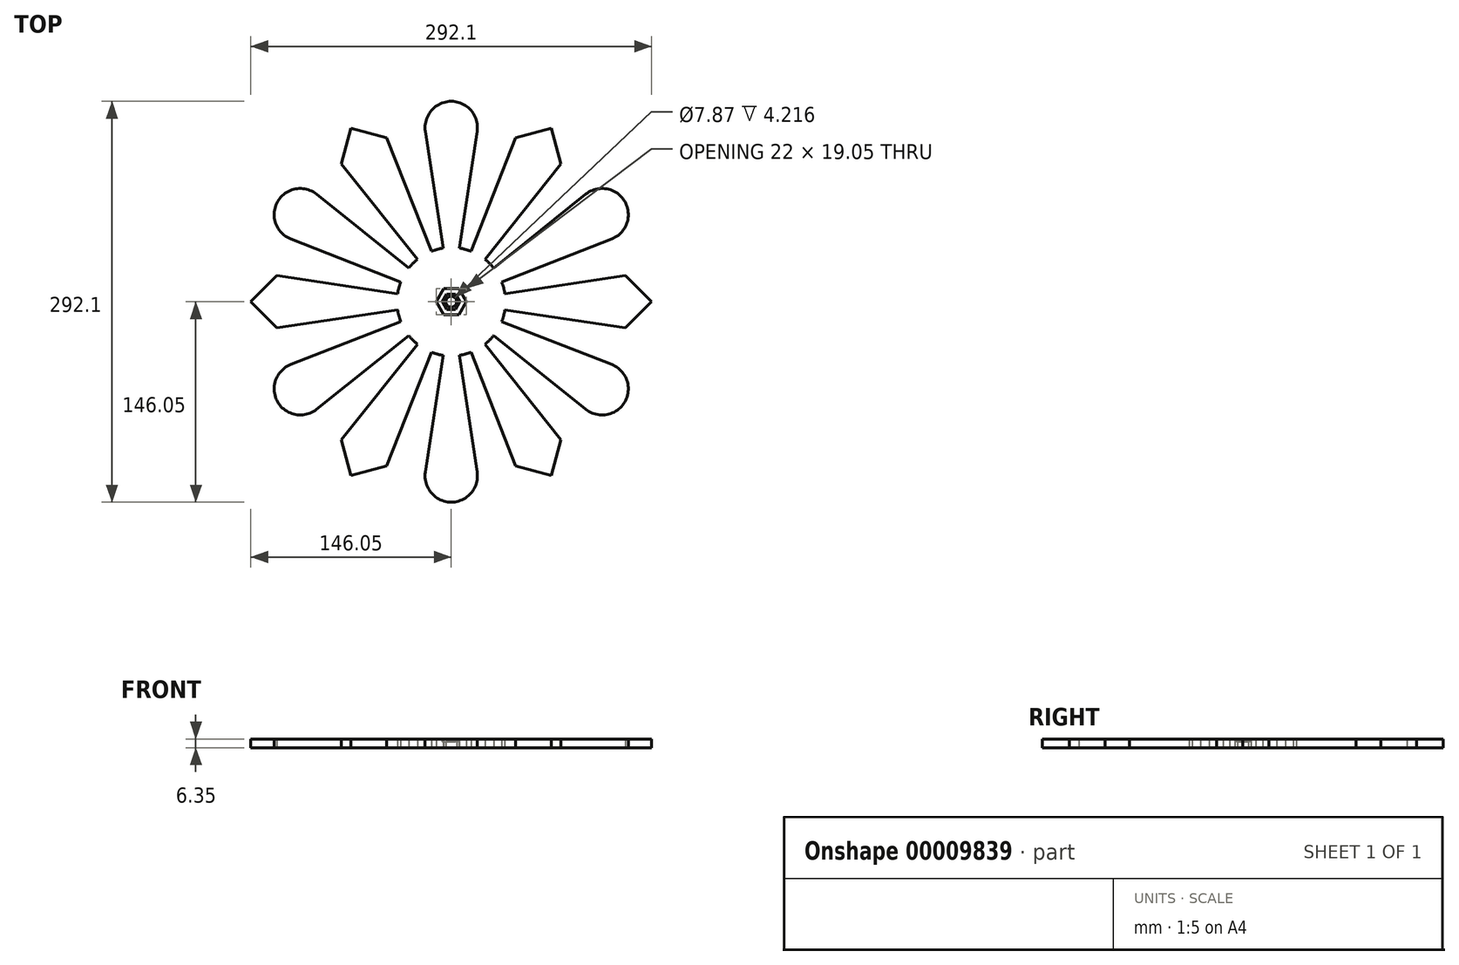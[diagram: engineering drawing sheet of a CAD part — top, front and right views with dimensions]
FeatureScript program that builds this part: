
annotation { "Feature Type Name" : "Feature", "Feature Type Description" : "" }
export const myFeature = defineFeature(function(context is Context, id is Id, definition is map)
    precondition{}
    {
        {
            var Q0;
            Q0=qCreatedBy(makeId("Top.planeOp"),FACE);
            var sketch = newSketch(context, id + "F0", { "sketchPlane" : qUnion([Q0])});
            skLineSegment(sketch, "E0.rect.bottom", {"start": v(203.2, 152.4) * mm, "end": v(-203.2, 152.4) * mm, "construction": true});
            skLineSegment(sketch, "E0.rect.top", {"start": v(203.2, -152.4) * mm, "end": v(-203.2, -152.4) * mm, "construction": true});
            skLineSegment(sketch, "E0.rect.left", {"start": v(203.2, 152.4) * mm, "end": v(203.2, -152.4) * mm, "construction": true});
            skLineSegment(sketch, "E0.rect.right", {"start": v(-203.2, 152.4) * mm, "end": v(-203.2, -152.4) * mm, "construction": true});
            skPoint(sketch, "E0.rect.middle", {"position": v(0, 0) * mm});
            skLineSegment(sketch, "E1.rect.bottom", {"start": v(27.94, 27.94) * mm, "end": v(-27.94, 27.94) * mm, "construction": true});
            skLineSegment(sketch, "E1.rect.top", {"start": v(27.94, -27.94) * mm, "end": v(-27.94, -27.94) * mm, "construction": true});
            skLineSegment(sketch, "E1.rect.left", {"start": v(27.94, 27.94) * mm, "end": v(27.94, -27.94) * mm, "construction": true});
            skLineSegment(sketch, "E1.rect.right", {"start": v(-27.94, 27.94) * mm, "end": v(-27.94, -27.94) * mm, "construction": true});
            skCircle(sketch, "E2", {"center": v(0, 0) * mm, "radius": 39.51 * mm});
            skCircle(sketch, "E3", {"center": v(0, 127) * mm, "radius": 19.05 * mm});
            skLineSegment(sketch, "E4.0", {"start": v(196.85, 146.05) * mm, "end": v(-196.85, 146.05) * mm, "construction": true});
            skLineSegment(sketch, "E4.1", {"start": v(196.85, 146.05) * mm, "end": v(196.85, -146.05) * mm, "construction": true});
            skLineSegment(sketch, "E4.2", {"start": v(196.85, -146.05) * mm, "end": v(-196.85, -146.05) * mm, "construction": true});
            skLineSegment(sketch, "E4.3", {"start": v(-196.85, 146.05) * mm, "end": v(-196.85, -146.05) * mm, "construction": true});
            skLineSegment(sketch, "E5", {"start": v(0, 0) * mm, "end": v(-18.83, 124.14) * mm});
            skLineSegment(sketch, "E6", {"start": v(0, 0) * mm, "end": v(18.83, 124.14) * mm});
            skLineSegment(sketch, "E7", {"start": v(47, 119.51) * mm, "end": v(80, 100.46) * mm});
            skLineSegment(sketch, "E8", {"start": v(80, 100.46) * mm, "end": v(0, 0) * mm});
            skLineSegment(sketch, "E9", {"start": v(47, 119.51) * mm, "end": v(0, 0) * mm});
            skPoint(sketch, "E10", {"position": v(63.5, 109.99) * mm});
            skLineSegment(sketch, "E11", {"start": v(63.5, 109.99) * mm, "end": v(0, 0) * mm, "construction": true});
            skLineSegment(sketch, "E12", {"start": v(0, 0) * mm, "end": v(0, 127) * mm, "construction": true});
            skLineSegment(sketch, "E13", {"start": v(47, 119.51) * mm, "end": v(73.03, 126.48) * mm});
            skLineSegment(sketch, "E14", {"start": v(73.03, 126.48) * mm, "end": v(80, 100.46) * mm});
            skLineSegment(sketch, "E15.1.0", {"start": v(-80, 100.46) * mm, "end": v(0, 0) * mm});
            skLineSegment(sketch, "E15.1.1", {"start": v(0, 0) * mm, "end": v(-109.99, 63.5) * mm, "construction": true});
            skLineSegment(sketch, "E15.1.2", {"start": v(-47, 119.51) * mm, "end": v(0, 0) * mm});
            skLineSegment(sketch, "E15.1.3", {"start": v(-73.03, 126.48) * mm, "end": v(-47, 119.51) * mm});
            skCircle(sketch, "E15.1.4", {"center": v(-109.99, 63.5) * mm, "radius": 19.05 * mm});
            skLineSegment(sketch, "E15.1.5", {"start": v(0, 0) * mm, "end": v(-98.1, 78.38) * mm});
            skLineSegment(sketch, "E15.1.6", {"start": v(-63.5, 109.99) * mm, "end": v(0, 0) * mm, "construction": true});
            skLineSegment(sketch, "E15.1.7", {"start": v(-80, 100.46) * mm, "end": v(-47, 119.51) * mm});
            skLineSegment(sketch, "E15.1.8", {"start": v(0, 0) * mm, "end": v(-116.93, 45.76) * mm});
            skLineSegment(sketch, "E15.1.9", {"start": v(-80, 100.46) * mm, "end": v(-73.03, 126.48) * mm});
            skPoint(sketch, "E15.1.10", {"position": v(-63.5, 109.99) * mm});
            skLineSegment(sketch, "E15.2.0", {"start": v(-127, -19.05) * mm, "end": v(0, 0) * mm});
            skLineSegment(sketch, "E15.2.1", {"start": v(0, 0) * mm, "end": v(-109.99, -63.5) * mm, "construction": true});
            skLineSegment(sketch, "E15.2.2", {"start": v(-127, 19.05) * mm, "end": v(0, 0) * mm});
            skLineSegment(sketch, "E15.2.3", {"start": v(-146.05, 0) * mm, "end": v(-127, 19.05) * mm});
            skCircle(sketch, "E15.2.4", {"center": v(-109.99, -63.5) * mm, "radius": 19.05 * mm});
            skLineSegment(sketch, "E15.2.5", {"start": v(0, 0) * mm, "end": v(-116.93, -45.76) * mm});
            skLineSegment(sketch, "E15.2.6", {"start": v(-127, 0) * mm, "end": v(0, 0) * mm, "construction": true});
            skLineSegment(sketch, "E15.2.7", {"start": v(-127, -19.05) * mm, "end": v(-127, 19.05) * mm});
            skLineSegment(sketch, "E15.2.8", {"start": v(0, 0) * mm, "end": v(-98.1, -78.38) * mm});
            skLineSegment(sketch, "E15.2.9", {"start": v(-127, -19.05) * mm, "end": v(-146.05, 0) * mm});
            skPoint(sketch, "E15.2.10", {"position": v(-127, 0) * mm});
            skLineSegment(sketch, "E15.3.0", {"start": v(-47, -119.51) * mm, "end": v(0, 0) * mm});
            skLineSegment(sketch, "E15.3.1", {"start": v(0, 0) * mm, "end": v(0, -127) * mm, "construction": true});
            skLineSegment(sketch, "E15.3.2", {"start": v(-80, -100.46) * mm, "end": v(0, 0) * mm});
            skLineSegment(sketch, "E15.3.3", {"start": v(-73.03, -126.48) * mm, "end": v(-80, -100.46) * mm});
            skCircle(sketch, "E15.3.4", {"center": v(0, -127) * mm, "radius": 19.05 * mm});
            skLineSegment(sketch, "E15.3.5", {"start": v(0, 0) * mm, "end": v(-18.83, -124.14) * mm});
            skLineSegment(sketch, "E15.3.6", {"start": v(-63.5, -109.99) * mm, "end": v(0, 0) * mm, "construction": true});
            skLineSegment(sketch, "E15.3.7", {"start": v(-47, -119.51) * mm, "end": v(-80, -100.46) * mm});
            skLineSegment(sketch, "E15.3.8", {"start": v(0, 0) * mm, "end": v(18.83, -124.14) * mm});
            skLineSegment(sketch, "E15.3.9", {"start": v(-47, -119.51) * mm, "end": v(-73.03, -126.48) * mm});
            skPoint(sketch, "E15.3.10", {"position": v(-63.5, -109.99) * mm});
            skLineSegment(sketch, "E15.4.0", {"start": v(80, -100.46) * mm, "end": v(0, 0) * mm});
            skLineSegment(sketch, "E15.4.1", {"start": v(0, 0) * mm, "end": v(109.99, -63.5) * mm, "construction": true});
            skLineSegment(sketch, "E15.4.2", {"start": v(47, -119.51) * mm, "end": v(0, 0) * mm});
            skLineSegment(sketch, "E15.4.3", {"start": v(73.03, -126.48) * mm, "end": v(47, -119.51) * mm});
            skCircle(sketch, "E15.4.4", {"center": v(109.99, -63.5) * mm, "radius": 19.05 * mm});
            skLineSegment(sketch, "E15.4.5", {"start": v(0, 0) * mm, "end": v(98.1, -78.38) * mm});
            skLineSegment(sketch, "E15.4.6", {"start": v(63.5, -109.99) * mm, "end": v(0, 0) * mm, "construction": true});
            skLineSegment(sketch, "E15.4.7", {"start": v(80, -100.46) * mm, "end": v(47, -119.51) * mm});
            skLineSegment(sketch, "E15.4.8", {"start": v(0, 0) * mm, "end": v(116.93, -45.76) * mm});
            skLineSegment(sketch, "E15.4.9", {"start": v(80, -100.46) * mm, "end": v(73.03, -126.48) * mm});
            skPoint(sketch, "E15.4.10", {"position": v(63.5, -109.99) * mm});
            skLineSegment(sketch, "E15.5.0", {"start": v(127, 19.05) * mm, "end": v(0, 0) * mm});
            skLineSegment(sketch, "E15.5.1", {"start": v(0, 0) * mm, "end": v(109.99, 63.5) * mm, "construction": true});
            skLineSegment(sketch, "E15.5.2", {"start": v(127, -19.05) * mm, "end": v(0, 0) * mm});
            skLineSegment(sketch, "E15.5.3", {"start": v(146.05, 0) * mm, "end": v(127, -19.05) * mm});
            skCircle(sketch, "E15.5.4", {"center": v(109.99, 63.5) * mm, "radius": 19.05 * mm});
            skLineSegment(sketch, "E15.5.5", {"start": v(0, 0) * mm, "end": v(116.93, 45.76) * mm});
            skLineSegment(sketch, "E15.5.6", {"start": v(127, 0) * mm, "end": v(0, 0) * mm, "construction": true});
            skLineSegment(sketch, "E15.5.7", {"start": v(127, 19.05) * mm, "end": v(127, -19.05) * mm});
            skLineSegment(sketch, "E15.5.8", {"start": v(0, 0) * mm, "end": v(98.1, 78.38) * mm});
            skLineSegment(sketch, "E15.5.9", {"start": v(127, 19.05) * mm, "end": v(146.05, 0) * mm});
            skPoint(sketch, "E15.5.10", {"position": v(127, 0) * mm});
            skSolve(sketch);
        }
        {
            var Q0;
            {var subQ1=sQuery(id+"F0.wireOp",EDGE,"E2");var subQ3=sQuery(id+"F0.wireOp",EDGE,"E15.2.0");var subQ5=makeQuery(id+"F0.imprint","INTERSECT",VERTEX,{"derivedFrom":[subQ1,subQ3]});Q0=makeQuery(id+"F0.imprint","IMPRINT",FACE,{"disambiguationData":[TD([[makeQuery(id+"F0.imprint","IMPRINT",EDGE,{"disambiguationData":[TD([[subQ5,-1.0]])],"derivedFrom":subQ1}),1.0]])]});}
            var Q1;
            {var subQ0=sQuery(id+"F0.wireOp",EDGE,"E6");var subQ1=sQuery(id+"F0.wireOp",EDGE,"E2");var subQ2=makeQuery(id+"F0.imprint","INTERSECT",VERTEX,{"derivedFrom":[subQ1,subQ0]});Q1=makeQuery(id+"F0.imprint","IMPRINT",FACE,{"disambiguationData":[TD([[makeQuery(id+"F0.imprint","IMPRINT",EDGE,{"disambiguationData":[TD([[subQ2,-1.0]])],"derivedFrom":subQ1}),-1.0]])]});}
            var Q2;
            {var subQ0=sQuery(id+"F0.wireOp",EDGE,"E9");var subQ1=sQuery(id+"F0.wireOp",EDGE,"E2");var subQ2=makeQuery(id+"F0.imprint","INTERSECT",VERTEX,{"derivedFrom":[subQ1,subQ0]});Q2=makeQuery(id+"F0.imprint","IMPRINT",FACE,{"disambiguationData":[TD([[makeQuery(id+"F0.imprint","IMPRINT",EDGE,{"disambiguationData":[TD([[subQ2,-1.0]])],"derivedFrom":subQ1}),1.0]])]});}
            var Q3;
            {var subQ0=sQuery(id+"F0.wireOp",EDGE,"E15.4.4");var subQ2=makeQuery(id+"F0.imprint","INTERSECT",VERTEX,{"derivedFrom":[subQ0,sQuery(id+"F0.wireOp",EDGE,"E15.4.5")]});Q3=makeQuery(id+"F0.imprint","IMPRINT",FACE,{"disambiguationData":[TD([[makeQuery(id+"F0.imprint","IMPRINT",EDGE,{"disambiguationData":[TD([[subQ2,1.0]])],"derivedFrom":subQ0}),1.0]])]});}
            var Q4;
            {var subQ1=sQuery(id+"F0.wireOp",EDGE,"E2");var subQ3=sQuery(id+"F0.wireOp",EDGE,"E15.2.8");var subQ5=makeQuery(id+"F0.imprint","INTERSECT",VERTEX,{"derivedFrom":[subQ1,subQ3]});Q4=makeQuery(id+"F0.imprint","IMPRINT",FACE,{"disambiguationData":[TD([[makeQuery(id+"F0.imprint","IMPRINT",EDGE,{"disambiguationData":[TD([[subQ5,-1.0]])],"derivedFrom":subQ1}),1.0]])]});}
            var Q5;
            {var subQ0=sQuery(id+"F0.wireOp",EDGE,"E15.1.2");var subQ1=sQuery(id+"F0.wireOp",EDGE,"E2");var subQ2=makeQuery(id+"F0.imprint","INTERSECT",VERTEX,{"derivedFrom":[subQ1,subQ0]});Q5=makeQuery(id+"F0.imprint","IMPRINT",FACE,{"disambiguationData":[TD([[makeQuery(id+"F0.imprint","IMPRINT",EDGE,{"disambiguationData":[TD([[subQ2,-1.0]])],"derivedFrom":subQ1}),1.0]])]});}
            var Q6;
            {var subQ0=sQuery(id+"F0.wireOp",EDGE,"E15.4.7");Q6=makeQuery(id+"F0.imprint","IMPRINT",FACE,{"disambiguationData":[TD([[makeQuery(id+"F0.imprint","IMPRINT",EDGE,{"derivedFrom":subQ0}),-1.0]])]});}
            var Q7;
            {var subQ0=sQuery(id+"F0.wireOp",EDGE,"E15.2.7");Q7=makeQuery(id+"F0.imprint","IMPRINT",FACE,{"disambiguationData":[TD([[makeQuery(id+"F0.imprint","IMPRINT",EDGE,{"derivedFrom":subQ0}),-1.0]])]});}
            var Q8;
            {var subQ1=sQuery(id+"F0.wireOp",EDGE,"E2");var subQ3=sQuery(id+"F0.wireOp",EDGE,"E15.1.0");var subQ5=makeQuery(id+"F0.imprint","INTERSECT",VERTEX,{"derivedFrom":[subQ1,subQ3]});Q8=makeQuery(id+"F0.imprint","IMPRINT",FACE,{"disambiguationData":[TD([[makeQuery(id+"F0.imprint","IMPRINT",EDGE,{"disambiguationData":[TD([[subQ5,-1.0]])],"derivedFrom":subQ1}),1.0]])]});}
            var Q9;
            {var subQ1=sQuery(id+"F0.wireOp",EDGE,"E2");var subQ3=sQuery(id+"F0.wireOp",EDGE,"E15.2.5");var subQ5=makeQuery(id+"F0.imprint","INTERSECT",VERTEX,{"derivedFrom":[subQ1,subQ3]});Q9=makeQuery(id+"F0.imprint","IMPRINT",FACE,{"disambiguationData":[TD([[makeQuery(id+"F0.imprint","IMPRINT",EDGE,{"disambiguationData":[TD([[subQ5,-1.0]])],"derivedFrom":subQ1}),1.0]])]});}
            var Q10;
            {var subQ1=sQuery(id+"F0.wireOp",EDGE,"E2");var subQ5=sQuery(id+"F0.wireOp",EDGE,"E15.3.5");var subQ6=makeQuery(id+"F0.imprint","INTERSECT",VERTEX,{"derivedFrom":[subQ1,subQ5]});Q10=makeQuery(id+"F0.imprint","IMPRINT",FACE,{"disambiguationData":[TD([[makeQuery(id+"F0.imprint","IMPRINT",EDGE,{"disambiguationData":[TD([[subQ6,-1.0]])],"derivedFrom":subQ1}),-1.0]])]});}
            var Q11;
            {var subQ1=sQuery(id+"F0.wireOp",EDGE,"E2");var subQ3=sQuery(id+"F0.wireOp",EDGE,"E15.1.8");var subQ5=makeQuery(id+"F0.imprint","INTERSECT",VERTEX,{"derivedFrom":[subQ1,subQ3]});Q11=makeQuery(id+"F0.imprint","IMPRINT",FACE,{"disambiguationData":[TD([[makeQuery(id+"F0.imprint","IMPRINT",EDGE,{"disambiguationData":[TD([[subQ5,-1.0]])],"derivedFrom":subQ1}),1.0]])]});}
            var Q12;
            {var subQ0=sQuery(id+"F0.wireOp",EDGE,"E6");var subQ1=sQuery(id+"F0.wireOp",EDGE,"E2");var subQ2=makeQuery(id+"F0.imprint","INTERSECT",VERTEX,{"derivedFrom":[subQ1,subQ0]});Q12=makeQuery(id+"F0.imprint","IMPRINT",FACE,{"disambiguationData":[TD([[makeQuery(id+"F0.imprint","IMPRINT",EDGE,{"disambiguationData":[TD([[subQ2,-1.0]])],"derivedFrom":subQ1}),1.0]])]});}
            var Q13;
            {var subQ1=sQuery(id+"F0.wireOp",EDGE,"E2");var subQ3=sQuery(id+"F0.wireOp",EDGE,"E15.5.0");var subQ5=makeQuery(id+"F0.imprint","INTERSECT",VERTEX,{"derivedFrom":[subQ1,subQ3]});Q13=makeQuery(id+"F0.imprint","IMPRINT",FACE,{"disambiguationData":[TD([[makeQuery(id+"F0.imprint","IMPRINT",EDGE,{"disambiguationData":[TD([[subQ5,1.0]])],"derivedFrom":subQ1}),1.0]])]});}
            var Q14;
            {var subQ0=sQuery(id+"F0.wireOp",EDGE,"E15.1.7");Q14=makeQuery(id+"F0.imprint","IMPRINT",FACE,{"disambiguationData":[TD([[makeQuery(id+"F0.imprint","IMPRINT",EDGE,{"derivedFrom":subQ0}),-1.0]])]});}
            var Q15;
            Q15=makeQuery(id+"F0.imprint","IMPRINT",FACE,{"disambiguationData":[TD([[makeQuery(id+"F0.imprint","IMPRINT",EDGE,{"derivedFrom":sQuery(id+"F0.wireOp",EDGE,"E7")}),1.0]])]});
            var Q16;
            {var subQ0=sQuery(id+"F0.wireOp",EDGE,"E15.5.7");Q16=makeQuery(id+"F0.imprint","IMPRINT",FACE,{"disambiguationData":[TD([[makeQuery(id+"F0.imprint","IMPRINT",EDGE,{"derivedFrom":subQ0}),-1.0]])]});}
            var Q17;
            {var subQ0=sQuery(id+"F0.wireOp",EDGE,"E15.2.2");var subQ1=sQuery(id+"F0.wireOp",EDGE,"E2");var subQ2=makeQuery(id+"F0.imprint","INTERSECT",VERTEX,{"derivedFrom":[subQ1,subQ0]});Q17=makeQuery(id+"F0.imprint","IMPRINT",FACE,{"disambiguationData":[TD([[makeQuery(id+"F0.imprint","IMPRINT",EDGE,{"disambiguationData":[TD([[subQ2,-1.0]])],"derivedFrom":subQ1}),1.0]])]});}
            var Q18;
            {var subQ1=sQuery(id+"F0.wireOp",EDGE,"E2");var subQ3=sQuery(id+"F0.wireOp",EDGE,"E15.1.5");var subQ5=makeQuery(id+"F0.imprint","INTERSECT",VERTEX,{"derivedFrom":[subQ1,subQ3]});Q18=makeQuery(id+"F0.imprint","IMPRINT",FACE,{"disambiguationData":[TD([[makeQuery(id+"F0.imprint","IMPRINT",EDGE,{"disambiguationData":[TD([[subQ5,-1.0]])],"derivedFrom":subQ1}),1.0]])]});}
            var Q19;
            Q19=makeQuery(id+"F0.imprint","IMPRINT",FACE,{"disambiguationData":[TD([[makeQuery(id+"F0.imprint","IMPRINT",EDGE,{"derivedFrom":sQuery(id+"F0.wireOp",EDGE,"E15.1.3")}),-1.0]])]});
            var Q20;
            {var subQ1=sQuery(id+"F0.wireOp",EDGE,"E2");var subQ3=sQuery(id+"F0.wireOp",EDGE,"E15.4.0");var subQ5=makeQuery(id+"F0.imprint","INTERSECT",VERTEX,{"derivedFrom":[subQ1,subQ3]});Q20=makeQuery(id+"F0.imprint","IMPRINT",FACE,{"disambiguationData":[TD([[makeQuery(id+"F0.imprint","IMPRINT",EDGE,{"disambiguationData":[TD([[subQ5,-1.0]])],"derivedFrom":subQ1}),1.0]])]});}
            var Q21;
            {var subQ1=sQuery(id+"F0.wireOp",EDGE,"E2");var subQ5=sQuery(id+"F0.wireOp",EDGE,"E15.4.5");var subQ6=makeQuery(id+"F0.imprint","INTERSECT",VERTEX,{"derivedFrom":[subQ1,subQ5]});Q21=makeQuery(id+"F0.imprint","IMPRINT",FACE,{"disambiguationData":[TD([[makeQuery(id+"F0.imprint","IMPRINT",EDGE,{"disambiguationData":[TD([[subQ6,-1.0]])],"derivedFrom":subQ1}),-1.0]])]});}
            var Q22;
            {var subQ0=sQuery(id+"F0.wireOp",EDGE,"E15.1.4");var subQ2=makeQuery(id+"F0.imprint","INTERSECT",VERTEX,{"derivedFrom":[subQ0,sQuery(id+"F0.wireOp",EDGE,"E15.1.5")]});Q22=makeQuery(id+"F0.imprint","IMPRINT",FACE,{"disambiguationData":[TD([[makeQuery(id+"F0.imprint","IMPRINT",EDGE,{"disambiguationData":[TD([[subQ2,1.0]])],"derivedFrom":subQ0}),1.0]])]});}
            var Q23;
            {var subQ1=sQuery(id+"F0.wireOp",EDGE,"E2");var subQ5=sQuery(id+"F0.wireOp",EDGE,"E15.5.5");var subQ6=makeQuery(id+"F0.imprint","INTERSECT",VERTEX,{"derivedFrom":[subQ1,subQ5]});Q23=makeQuery(id+"F0.imprint","IMPRINT",FACE,{"disambiguationData":[TD([[makeQuery(id+"F0.imprint","IMPRINT",EDGE,{"disambiguationData":[TD([[subQ6,-1.0]])],"derivedFrom":subQ1}),-1.0]])]});}
            var Q24;
            {var subQ1=sQuery(id+"F0.wireOp",EDGE,"E2");var subQ3=sQuery(id+"F0.wireOp",EDGE,"E15.3.0");var subQ5=makeQuery(id+"F0.imprint","INTERSECT",VERTEX,{"derivedFrom":[subQ1,subQ3]});Q24=makeQuery(id+"F0.imprint","IMPRINT",FACE,{"disambiguationData":[TD([[makeQuery(id+"F0.imprint","IMPRINT",EDGE,{"disambiguationData":[TD([[subQ5,-1.0]])],"derivedFrom":subQ1}),1.0]])]});}
            var Q25;
            {var subQ1=sQuery(id+"F0.wireOp",EDGE,"E2");var subQ3=sQuery(id+"F0.wireOp",EDGE,"E15.3.5");var subQ5=makeQuery(id+"F0.imprint","INTERSECT",VERTEX,{"derivedFrom":[subQ1,subQ3]});Q25=makeQuery(id+"F0.imprint","IMPRINT",FACE,{"disambiguationData":[TD([[makeQuery(id+"F0.imprint","IMPRINT",EDGE,{"disambiguationData":[TD([[subQ5,-1.0]])],"derivedFrom":subQ1}),1.0]])]});}
            var Q26;
            {var subQ1=sQuery(id+"F0.wireOp",EDGE,"E2");var subQ3=sQuery(id+"F0.wireOp",EDGE,"E15.5.5");var subQ5=makeQuery(id+"F0.imprint","INTERSECT",VERTEX,{"derivedFrom":[subQ1,subQ3]});Q26=makeQuery(id+"F0.imprint","IMPRINT",FACE,{"disambiguationData":[TD([[makeQuery(id+"F0.imprint","IMPRINT",EDGE,{"disambiguationData":[TD([[subQ5,-1.0]])],"derivedFrom":subQ1}),1.0]])]});}
            var Q27;
            {var subQ0=sQuery(id+"F0.wireOp",EDGE,"E15.5.8");var subQ1=sQuery(id+"F0.wireOp",EDGE,"E2");var subQ2=makeQuery(id+"F0.imprint","INTERSECT",VERTEX,{"derivedFrom":[subQ1,subQ0]});Q27=makeQuery(id+"F0.imprint","IMPRINT",FACE,{"disambiguationData":[TD([[makeQuery(id+"F0.imprint","IMPRINT",EDGE,{"disambiguationData":[TD([[subQ2,-1.0]])],"derivedFrom":subQ1}),1.0]])]});}
            var Q28;
            {var subQ0=sQuery(id+"F0.wireOp",EDGE,"E3");var subQ2=makeQuery(id+"F0.imprint","INTERSECT",VERTEX,{"derivedFrom":[subQ0,sQuery(id+"F0.wireOp",EDGE,"E5")]});Q28=makeQuery(id+"F0.imprint","IMPRINT",FACE,{"disambiguationData":[TD([[makeQuery(id+"F0.imprint","IMPRINT",EDGE,{"disambiguationData":[TD([[subQ2,-1.0]])],"derivedFrom":subQ0}),1.0]])]});}
            var Q29;
            Q29=makeQuery(id+"F0.imprint","IMPRINT",FACE,{"disambiguationData":[TD([[makeQuery(id+"F0.imprint","IMPRINT",EDGE,{"derivedFrom":sQuery(id+"F0.wireOp",EDGE,"E15.3.3")}),-1.0]])]});
            var Q30;
            {var subQ0=sQuery(id+"F0.wireOp",EDGE,"E15.2.5");var subQ1=sQuery(id+"F0.wireOp",EDGE,"E2");var subQ2=makeQuery(id+"F0.imprint","INTERSECT",VERTEX,{"derivedFrom":[subQ1,subQ0]});Q30=makeQuery(id+"F0.imprint","IMPRINT",FACE,{"disambiguationData":[TD([[makeQuery(id+"F0.imprint","IMPRINT",EDGE,{"disambiguationData":[TD([[subQ2,-1.0]])],"derivedFrom":subQ1}),-1.0]])]});}
            var Q31;
            Q31=makeQuery(id+"F0.imprint","IMPRINT",FACE,{"disambiguationData":[TD([[makeQuery(id+"F0.imprint","IMPRINT",EDGE,{"derivedFrom":sQuery(id+"F0.wireOp",EDGE,"E15.5.3")}),-1.0]])]});
            var Q32;
            {var subQ0=sQuery(id+"F0.wireOp",EDGE,"E15.5.4");var subQ2=makeQuery(id+"F0.imprint","INTERSECT",VERTEX,{"derivedFrom":[subQ0,sQuery(id+"F0.wireOp",EDGE,"E15.5.5")]});Q32=makeQuery(id+"F0.imprint","IMPRINT",FACE,{"disambiguationData":[TD([[makeQuery(id+"F0.imprint","IMPRINT",EDGE,{"disambiguationData":[TD([[subQ2,1.0]])],"derivedFrom":subQ0}),1.0]])]});}
            var Q33;
            {var subQ0=sQuery(id+"F0.wireOp",EDGE,"E15.5.5");var subQ1=sQuery(id+"F0.wireOp",EDGE,"E2");var subQ2=makeQuery(id+"F0.imprint","INTERSECT",VERTEX,{"derivedFrom":[subQ1,subQ0]});Q33=makeQuery(id+"F0.imprint","IMPRINT",FACE,{"disambiguationData":[TD([[makeQuery(id+"F0.imprint","IMPRINT",EDGE,{"disambiguationData":[TD([[subQ2,1.0]])],"derivedFrom":subQ1}),1.0]])]});}
            var Q34;
            {var subQ0=sQuery(id+"F0.wireOp",EDGE,"E15.4.2");var subQ1=sQuery(id+"F0.wireOp",EDGE,"E2");var subQ2=makeQuery(id+"F0.imprint","INTERSECT",VERTEX,{"derivedFrom":[subQ1,subQ0]});Q34=makeQuery(id+"F0.imprint","IMPRINT",FACE,{"disambiguationData":[TD([[makeQuery(id+"F0.imprint","IMPRINT",EDGE,{"disambiguationData":[TD([[subQ2,-1.0]])],"derivedFrom":subQ1}),1.0]])]});}
            var Q35;
            {var subQ1=sQuery(id+"F0.wireOp",EDGE,"E2");var subQ3=sQuery(id+"F0.wireOp",EDGE,"E5");var subQ5=makeQuery(id+"F0.imprint","INTERSECT",VERTEX,{"derivedFrom":[subQ1,subQ3]});Q35=makeQuery(id+"F0.imprint","IMPRINT",FACE,{"disambiguationData":[TD([[makeQuery(id+"F0.imprint","IMPRINT",EDGE,{"disambiguationData":[TD([[subQ5,-1.0]])],"derivedFrom":subQ1}),1.0]])]});}
            var Q36;
            {var subQ3=sQuery(id+"F0.wireOp",EDGE,"E7");Q36=makeQuery(id+"F0.imprint","IMPRINT",FACE,{"disambiguationData":[TD([[makeQuery(id+"F0.imprint","IMPRINT",EDGE,{"derivedFrom":subQ3}),-1.0]])]});}
            var Q37;
            {var subQ1=sQuery(id+"F0.wireOp",EDGE,"E2");var subQ3=sQuery(id+"F0.wireOp",EDGE,"E15.4.8");var subQ5=makeQuery(id+"F0.imprint","INTERSECT",VERTEX,{"derivedFrom":[subQ1,subQ3]});Q37=makeQuery(id+"F0.imprint","IMPRINT",FACE,{"disambiguationData":[TD([[makeQuery(id+"F0.imprint","IMPRINT",EDGE,{"disambiguationData":[TD([[subQ5,-1.0]])],"derivedFrom":subQ1}),1.0]])]});}
            var Q38;
            {var subQ0=sQuery(id+"F0.wireOp",EDGE,"E15.3.2");var subQ1=sQuery(id+"F0.wireOp",EDGE,"E2");var subQ2=makeQuery(id+"F0.imprint","INTERSECT",VERTEX,{"derivedFrom":[subQ1,subQ0]});Q38=makeQuery(id+"F0.imprint","IMPRINT",FACE,{"disambiguationData":[TD([[makeQuery(id+"F0.imprint","IMPRINT",EDGE,{"disambiguationData":[TD([[subQ2,-1.0]])],"derivedFrom":subQ1}),1.0]])]});}
            var Q39;
            {var subQ0=sQuery(id+"F0.wireOp",EDGE,"E15.3.7");Q39=makeQuery(id+"F0.imprint","IMPRINT",FACE,{"disambiguationData":[TD([[makeQuery(id+"F0.imprint","IMPRINT",EDGE,{"derivedFrom":subQ0}),-1.0]])]});}
            var Q40;
            {var subQ1=sQuery(id+"F0.wireOp",EDGE,"E2");var subQ3=sQuery(id+"F0.wireOp",EDGE,"E8");var subQ5=makeQuery(id+"F0.imprint","INTERSECT",VERTEX,{"derivedFrom":[subQ1,subQ3]});Q40=makeQuery(id+"F0.imprint","IMPRINT",FACE,{"disambiguationData":[TD([[makeQuery(id+"F0.imprint","IMPRINT",EDGE,{"disambiguationData":[TD([[subQ5,-1.0]])],"derivedFrom":subQ1}),1.0]])]});}
            var Q41;
            {var subQ1=sQuery(id+"F0.wireOp",EDGE,"E2");var subQ5=sQuery(id+"F0.wireOp",EDGE,"E15.1.5");var subQ6=makeQuery(id+"F0.imprint","INTERSECT",VERTEX,{"derivedFrom":[subQ1,subQ5]});Q41=makeQuery(id+"F0.imprint","IMPRINT",FACE,{"disambiguationData":[TD([[makeQuery(id+"F0.imprint","IMPRINT",EDGE,{"disambiguationData":[TD([[subQ6,-1.0]])],"derivedFrom":subQ1}),-1.0]])]});}
            var Q42;
            {var subQ1=sQuery(id+"F0.wireOp",EDGE,"E2");var subQ3=sQuery(id+"F0.wireOp",EDGE,"E15.4.5");var subQ5=makeQuery(id+"F0.imprint","INTERSECT",VERTEX,{"derivedFrom":[subQ1,subQ3]});Q42=makeQuery(id+"F0.imprint","IMPRINT",FACE,{"disambiguationData":[TD([[makeQuery(id+"F0.imprint","IMPRINT",EDGE,{"disambiguationData":[TD([[subQ5,-1.0]])],"derivedFrom":subQ1}),1.0]])]});}
            var Q43;
            {var subQ1=sQuery(id+"F0.wireOp",EDGE,"E2");var subQ3=sQuery(id+"F0.wireOp",EDGE,"E15.3.8");var subQ5=makeQuery(id+"F0.imprint","INTERSECT",VERTEX,{"derivedFrom":[subQ1,subQ3]});Q43=makeQuery(id+"F0.imprint","IMPRINT",FACE,{"disambiguationData":[TD([[makeQuery(id+"F0.imprint","IMPRINT",EDGE,{"disambiguationData":[TD([[subQ5,-1.0]])],"derivedFrom":subQ1}),1.0]])]});}
            var Q44;
            Q44=makeQuery(id+"F0.imprint","IMPRINT",FACE,{"disambiguationData":[TD([[makeQuery(id+"F0.imprint","IMPRINT",EDGE,{"derivedFrom":sQuery(id+"F0.wireOp",EDGE,"E15.4.3")}),-1.0]])]});
            var Q45;
            Q45=makeQuery(id+"F0.imprint","IMPRINT",FACE,{"disambiguationData":[TD([[makeQuery(id+"F0.imprint","IMPRINT",EDGE,{"derivedFrom":sQuery(id+"F0.wireOp",EDGE,"E15.2.3")}),-1.0]])]});
            var Q46;
            {var subQ0=sQuery(id+"F0.wireOp",EDGE,"E15.2.4");var subQ2=makeQuery(id+"F0.imprint","INTERSECT",VERTEX,{"derivedFrom":[subQ0,sQuery(id+"F0.wireOp",EDGE,"E15.2.5")]});Q46=makeQuery(id+"F0.imprint","IMPRINT",FACE,{"disambiguationData":[TD([[makeQuery(id+"F0.imprint","IMPRINT",EDGE,{"disambiguationData":[TD([[subQ2,1.0]])],"derivedFrom":subQ0}),1.0]])]});}
            var Q47;
            {var subQ0=sQuery(id+"F0.wireOp",EDGE,"E15.3.4");var subQ2=makeQuery(id+"F0.imprint","INTERSECT",VERTEX,{"derivedFrom":[subQ0,sQuery(id+"F0.wireOp",EDGE,"E15.3.5")]});Q47=makeQuery(id+"F0.imprint","IMPRINT",FACE,{"disambiguationData":[TD([[makeQuery(id+"F0.imprint","IMPRINT",EDGE,{"disambiguationData":[TD([[subQ2,1.0]])],"derivedFrom":subQ0}),1.0]])]});}
            extrude(context, id + "F1", {"entities" : qUnion([Q0, Q1, Q2, Q3, Q4, Q5, Q6, Q7, Q8, Q9, Q10, Q11, Q12, Q13, Q14, Q15, Q16, Q17, Q18, Q19, Q20, Q21, Q22, Q23, Q24, Q25, Q26, Q27, Q28, Q29, Q30, Q31, Q32, Q33, Q34, Q35, Q36, Q37, Q38, Q39, Q40, Q41, Q42, Q43, Q44, Q45, Q46, Q47]), "depth" : 6.35 * mm});
        }
        {
            var Q0;
            Q0=qCreatedBy(makeId("Top.planeOp"),FACE);
            var sketch = newSketch(context, id + "F2", { "sketchPlane" : qUnion([Q0])});
            skCircle(sketch, "E16", {"center": v(0, 0) * mm, "radius": 9.53 * mm, "construction": true});
            skLineSegment(sketch, "E17.0", {"start": v(-5.5, 9.53) * mm, "end": v(5.5, 9.53) * mm});
            skLineSegment(sketch, "E17.1", {"start": v(5.5, 9.52) * mm, "end": v(11, 0) * mm});
            skLineSegment(sketch, "E17.2", {"start": v(11, 0) * mm, "end": v(5.5, -9.52) * mm});
            skLineSegment(sketch, "E17.3", {"start": v(5.5, -9.52) * mm, "end": v(-5.5, -9.53) * mm});
            skLineSegment(sketch, "E17.4", {"start": v(-5.5, -9.53) * mm, "end": v(-11, 0) * mm});
            skLineSegment(sketch, "E17.5", {"start": v(-11, 0) * mm, "end": v(-5.5, 9.52) * mm});
            skPoint(sketch, "E17.0.midPoint", {"position": v(0, 9.53) * mm});
            skSolve(sketch);
        }
        {
            var Q0;
            Q0=makeQuery(id+"F2.imprint","IMPRINT",FACE,{"disambiguationData":[TD([[makeQuery(id+"F2.imprint","IMPRINT",EDGE,{"derivedFrom":sQuery(id+"F2.wireOp",EDGE,"E17.0")}),-1.0]])]});
            extrude(context, id + "F3", {"entities" : qUnion([Q0]), "operationType" : NewBodyOperationType.REMOVE, "endBound" : BoundingType.THROUGH_ALL, "depth" : 25.4 * mm});
        }
        {
            var Q0;
            Q0=qCreatedBy(makeId("Top.planeOp"),FACE);
            var sketch = newSketch(context, id + "F4", { "sketchPlane" : qUnion([Q0])});
            skLineSegment(sketch, "E18.0", {"start": v(-5.5, -9.53) * mm, "end": v(-11, 0) * mm});
            skLineSegment(sketch, "E19.0", {"start": v(5.5, -9.52) * mm, "end": v(-5.5, -9.53) * mm});
            skLineSegment(sketch, "E20.0", {"start": v(11, 0) * mm, "end": v(5.5, -9.52) * mm});
            skLineSegment(sketch, "E21.0", {"start": v(5.5, 9.53) * mm, "end": v(11, 0) * mm});
            skLineSegment(sketch, "E22.0", {"start": v(-5.5, 9.53) * mm, "end": v(5.5, 9.53) * mm});
            skLineSegment(sketch, "E23.0", {"start": v(-11, 0) * mm, "end": v(-5.5, 9.52) * mm});
            skCircle(sketch, "E24", {"center": v(0, 0) * mm, "radius": 3.94 * mm});
            skSolve(sketch);
        }
        {
            var Q0;
            Q0=makeQuery(id+"F4.imprint","IMPRINT",FACE,{"disambiguationData":[TD([[makeQuery(id+"F4.imprint","IMPRINT",EDGE,{"derivedFrom":sQuery(id+"F4.wireOp",EDGE,"E18.0")}),-1.0]])]});
            var Q1;
            Q1=makeQuery(id+"F1.opExtrude","CAP_FACE",FACE,{"disambiguationData":[OSD([sQuery(id+"F0.wireOp",EDGE,"E2"),sQuery(id+"F0.wireOp",EDGE,"E3"),sQuery(id+"F0.wireOp",EDGE,"E5"),sQuery(id+"F0.wireOp",EDGE,"E6"),sQuery(id+"F0.wireOp",EDGE,"E8"),sQuery(id+"F0.wireOp",EDGE,"E9"),sQuery(id+"F0.wireOp",EDGE,"E13"),sQuery(id+"F0.wireOp",EDGE,"E14"),sQuery(id+"F0.wireOp",EDGE,"E15.1.0"),sQuery(id+"F0.wireOp",EDGE,"E15.1.2"),sQuery(id+"F0.wireOp",EDGE,"E15.1.3"),sQuery(id+"F0.wireOp",EDGE,"E15.1.4"),sQuery(id+"F0.wireOp",EDGE,"E15.1.5"),sQuery(id+"F0.wireOp",EDGE,"E15.1.8"),sQuery(id+"F0.wireOp",EDGE,"E15.1.9"),sQuery(id+"F0.wireOp",EDGE,"E15.2.0"),sQuery(id+"F0.wireOp",EDGE,"E15.2.2"),sQuery(id+"F0.wireOp",EDGE,"E15.2.3"),sQuery(id+"F0.wireOp",EDGE,"E15.2.4"),sQuery(id+"F0.wireOp",EDGE,"E15.2.5"),sQuery(id+"F0.wireOp",EDGE,"E15.2.8"),sQuery(id+"F0.wireOp",EDGE,"E15.2.9"),sQuery(id+"F0.wireOp",EDGE,"E15.3.0"),sQuery(id+"F0.wireOp",EDGE,"E15.3.2"),sQuery(id+"F0.wireOp",EDGE,"E15.3.3"),sQuery(id+"F0.wireOp",EDGE,"E15.3.4"),sQuery(id+"F0.wireOp",EDGE,"E15.3.5"),sQuery(id+"F0.wireOp",EDGE,"E15.3.8"),sQuery(id+"F0.wireOp",EDGE,"E15.3.9"),sQuery(id+"F0.wireOp",EDGE,"E15.4.0"),sQuery(id+"F0.wireOp",EDGE,"E15.4.2"),sQuery(id+"F0.wireOp",EDGE,"E15.4.3"),sQuery(id+"F0.wireOp",EDGE,"E15.4.4"),sQuery(id+"F0.wireOp",EDGE,"E15.4.5"),sQuery(id+"F0.wireOp",EDGE,"E15.4.8"),sQuery(id+"F0.wireOp",EDGE,"E15.4.9"),sQuery(id+"F0.wireOp",EDGE,"E15.5.0"),sQuery(id+"F0.wireOp",EDGE,"E15.5.2"),sQuery(id+"F0.wireOp",EDGE,"E15.5.3"),sQuery(id+"F0.wireOp",EDGE,"E15.5.4"),sQuery(id+"F0.wireOp",EDGE,"E15.5.5"),sQuery(id+"F0.wireOp",EDGE,"E15.5.8"),sQuery(id+"F0.wireOp",EDGE,"E15.5.9")])],"isStart":false});
            extrude(context, id + "F5", {"entities" : qUnion([Q0]), "endBound" : BoundingType.UP_TO_SURFACE, "endBoundEntityFace" : qUnion([Q1]), "depth" : 25.4 * mm});
        }
        {
            var Q0;
            Q0=makeQuery(id+"F5.opExtrude","CAP_FACE",FACE,{"disambiguationData":[OSD([sQuery(id+"F4.wireOp",EDGE,"E18.0"),sQuery(id+"F4.wireOp",EDGE,"E19.0"),sQuery(id+"F4.wireOp",EDGE,"E20.0"),sQuery(id+"F4.wireOp",EDGE,"E21.0"),sQuery(id+"F4.wireOp",EDGE,"E22.0"),sQuery(id+"F4.wireOp",EDGE,"E23.0"),sQuery(id+"F4.wireOp",EDGE,"E24")])],"isStart":false});
            var sketch = newSketch(context, id + "F6", { "sketchPlane" : qUnion([Q0])});
            skCircle(sketch, "E25", {"center": v(0, 0) * mm, "radius": 6.35 * mm, "construction": true});
            skLineSegment(sketch, "E26.0", {"start": v(6.35, 0) * mm, "end": v(3.18, -5.5) * mm});
            skLineSegment(sketch, "E26.1", {"start": v(3.18, -5.5) * mm, "end": v(-3.17, -5.5) * mm});
            skLineSegment(sketch, "E26.2", {"start": v(-3.17, -5.5) * mm, "end": v(-6.35, 0) * mm});
            skLineSegment(sketch, "E26.3", {"start": v(-6.35, 0) * mm, "end": v(-3.18, 5.5) * mm});
            skLineSegment(sketch, "E26.4", {"start": v(-3.18, 5.5) * mm, "end": v(3.17, 5.5) * mm});
            skLineSegment(sketch, "E26.5", {"start": v(3.17, 5.5) * mm, "end": v(6.35, 0) * mm});
            skSolve(sketch);
        }
        {
            var Q0;
            Q0=makeQuery(id+"F6.imprint","IMPRINT",FACE,{"disambiguationData":[TD([[makeQuery(id+"F6.imprint","IMPRINT",EDGE,{"derivedFrom":sQuery(id+"F6.wireOp",EDGE,"E26.0")}),-1.0]])]});
            extrude(context, id + "F7", {"entities" : qUnion([Q0]), "operationType" : NewBodyOperationType.REMOVE, "oppositeDirection" : true, "depth" : 2.13 * mm});
        }
    });
